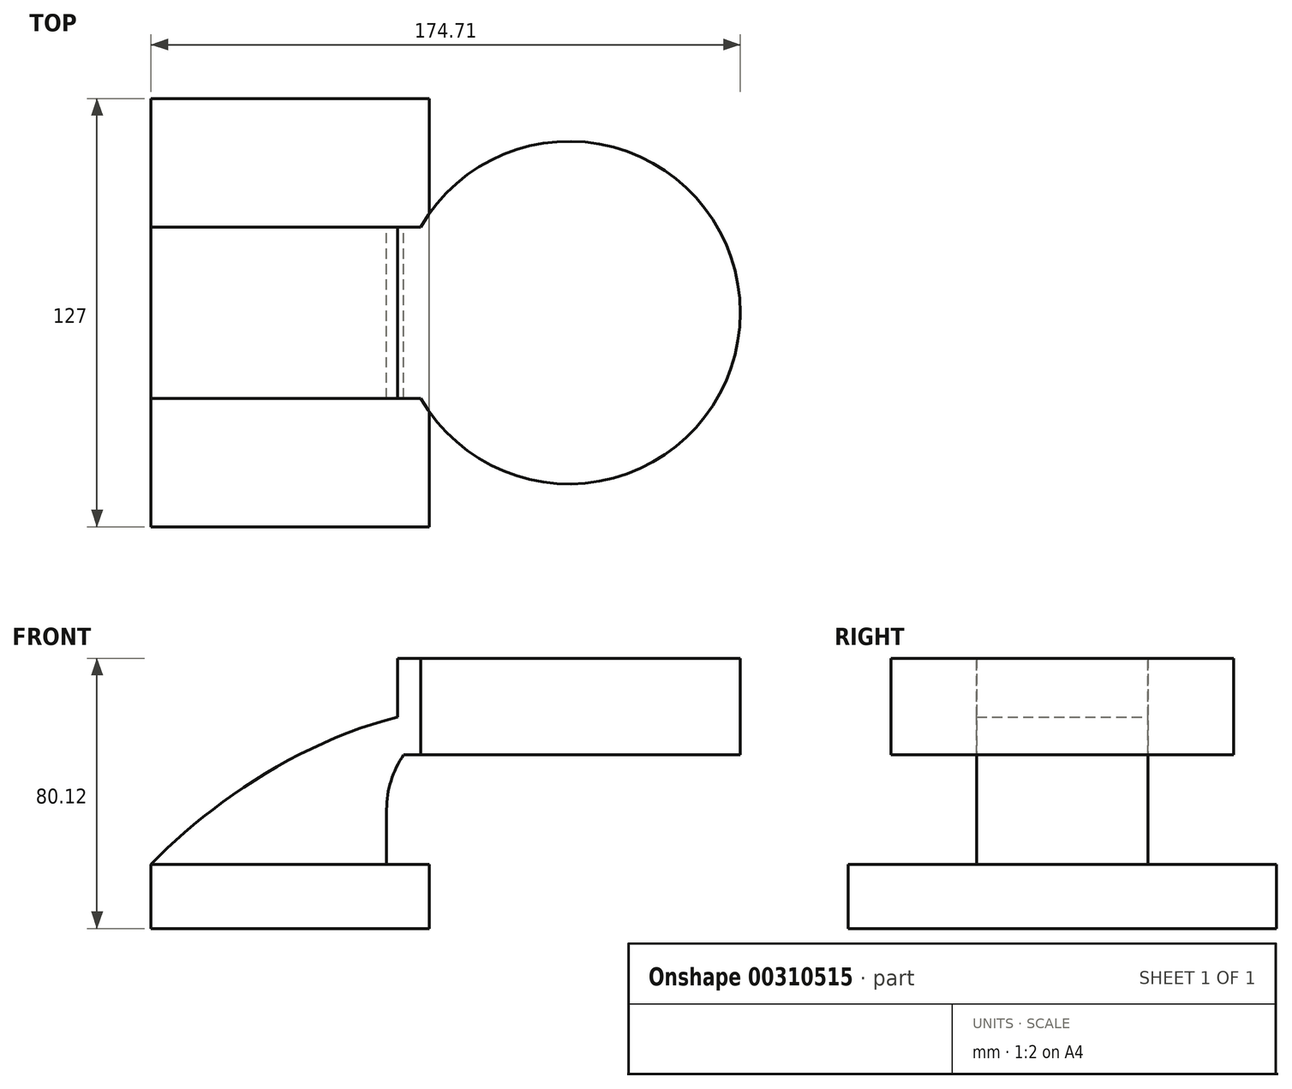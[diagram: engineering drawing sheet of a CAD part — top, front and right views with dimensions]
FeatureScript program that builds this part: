
annotation { "Feature Type Name" : "Feature", "Feature Type Description" : "" }
export const myFeature = defineFeature(function(context is Context, id is Id, definition is map)
    precondition{}
    {
        {
            var Q0;
            Q0=qCreatedBy(makeId("Front.planeOp"),FACE);
            var sketch = newSketch(context, id + "F0", { "sketchPlane" : qUnion([Q0])});
            skLineSegment(sketch, "E0.bottom", {"start": v(-41.28, 9.52) * mm, "end": v(41.27, 9.53) * mm});
            skLineSegment(sketch, "E0.top", {"start": v(-41.28, -9.53) * mm, "end": v(41.28, -9.53) * mm});
            skLineSegment(sketch, "E0.left", {"start": v(-41.28, 9.52) * mm, "end": v(-41.27, -9.53) * mm});
            skLineSegment(sketch, "E0.right", {"start": v(41.28, 9.53) * mm, "end": v(41.28, -9.52) * mm});
            skPoint(sketch, "E0.middle", {"position": v(0, 0) * mm});
            skLineSegment(sketch, "E1.bottom", {"start": v(82.63, 42.02) * mm, "end": v(31.83, 42.02) * mm});
            skLineSegment(sketch, "E1.top", {"start": v(82.63, 70.6) * mm, "end": v(31.83, 70.6) * mm});
            skLineSegment(sketch, "E1.left", {"start": v(82.63, 42.02) * mm, "end": v(82.63, 70.6) * mm});
            skLineSegment(sketch, "E1.right", {"start": v(31.83, 42.02) * mm, "end": v(31.83, 70.6) * mm});
            skPoint(sketch, "E1.middle", {"position": v(57.23, 56.3) * mm});
            skLineSegment(sketch, "E2", {"start": v(41.27, 9.53) * mm, "end": v(41.27, 25.76) * mm});
            skArc(sketch, "E3", {"start": v(41.27, 25.76) * mm, "mid": v(45.95, 37.04) * mm, "end": v(57.23, 41.72) * mm});
            skPoint(sketch, "E3.endSnap0", {"position": v(57.23, 42.02) * mm});
            skLineSegment(sketch, "E4", {"start": v(57.23, 41.72) * mm, "end": v(109.63, 41.72) * mm});
            skArc(sketch, "E5.0", {"start": v(28.57, 25.76) * mm, "mid": v(36.97, 46.02) * mm, "end": v(57.23, 54.42) * mm});
            skLineSegment(sketch, "E6", {"start": v(28.57, 25.76) * mm, "end": v(28.57, 9.53) * mm});
            skFitSpline(sketch, "E7", {"points": [v(-41.28, 9.53) * mm, v(57.23, 56.3) * mm], "startDerivative": vector(67.41, 69.91) * mm, "endDerivative": vector(113.5, -1.17) * mm});
            skSolve(sketch);
        }
        {
            var Q0;
            Q0=makeQuery(id+"F0.imprint","IMPRINT",FACE,{"disambiguationData":[TD([[makeQuery(id+"F0.imprint","IMPRINT",EDGE,{"derivedFrom":sQuery(id+"F0.wireOp",EDGE,"E0.top")}),1.0]])]});
            extrude(context, id + "F1", {"entities" : qUnion([Q0]), "endBound" : BoundingType.SYMMETRIC, "depth" : 127 * mm});
        }
        {
            var Q0;
            {var subQ5=sQuery(id+"F0.wireOp",EDGE,"E6");Q0=makeQuery(id+"F0.imprint","IMPRINT",FACE,{"disambiguationData":[TD([[makeQuery(id+"F0.imprint","IMPRINT",EDGE,{"derivedFrom":subQ5}),-1.0]])]});}
            extrude(context, id + "F2", {"entities" : qUnion([Q0]), "operationType" : NewBodyOperationType.ADD, "endBound" : BoundingType.SYMMETRIC, "depth" : 50.8 * mm});
        }
        {
            var Q0;
            {var subQ1=sQuery(id+"F0.wireOp",EDGE,"E1.top");Q0=makeQuery(id+"F0.imprint","IMPRINT",FACE,{"disambiguationData":[TD([[makeQuery(id+"F0.imprint","IMPRINT",EDGE,{"derivedFrom":subQ1}),1.0]])]});}
            var Q1;
            Q1 = qSketchRegion(id + "F4", true);
            var Q2;
            Q2 = qSketchRegion(id + "F5", true);
            extrude(context, id + "F3", {"entities" : qUnion([Q0, Q1, Q2]), "operationType" : NewBodyOperationType.ADD, "endBound" : BoundingType.SYMMETRIC, "depth" : 50.8 * mm});
        }
        {
            var Q0;
            Q0=qCreatedBy(makeId("Front.planeOp"),FACE);
            var sketch = newSketch(context, id + "F4", { "sketchPlane" : qUnion([Q0])});
            skSolve(sketch);
        }
        {
            var Q0;
            Q0=makeQuery(id+"F3.opExtrude","SWEPT_FACE",FACE,{"disambiguationData":[OSD([sQuery(id+"F0.wireOp",EDGE,"E1.right")])]});
            var sketch = newSketch(context, id + "F5", { "sketchPlane" : qUnion([Q0])});
            skSolve(sketch);
        }
        {
            var Q0;
            {var subQ1=sQuery(id+"F0.wireOp",EDGE,"E1.top");Q0=makeQuery(id+"F0.imprint","IMPRINT",FACE,{"disambiguationData":[TD([[makeQuery(id+"F0.imprint","IMPRINT",EDGE,{"derivedFrom":subQ1}),1.0]])]});}
            var Q1;
            Q1=sQuery(id+"F0.wireOp",EDGE,"E1.left");
            revolve(context, id + "F6", {"operationType" : NewBodyOperationType.ADD, "entities" : qUnion([Q0]), "axis" : qUnion([Q1]), "revolveType" : RevolveType.FULL});
        }
    });
